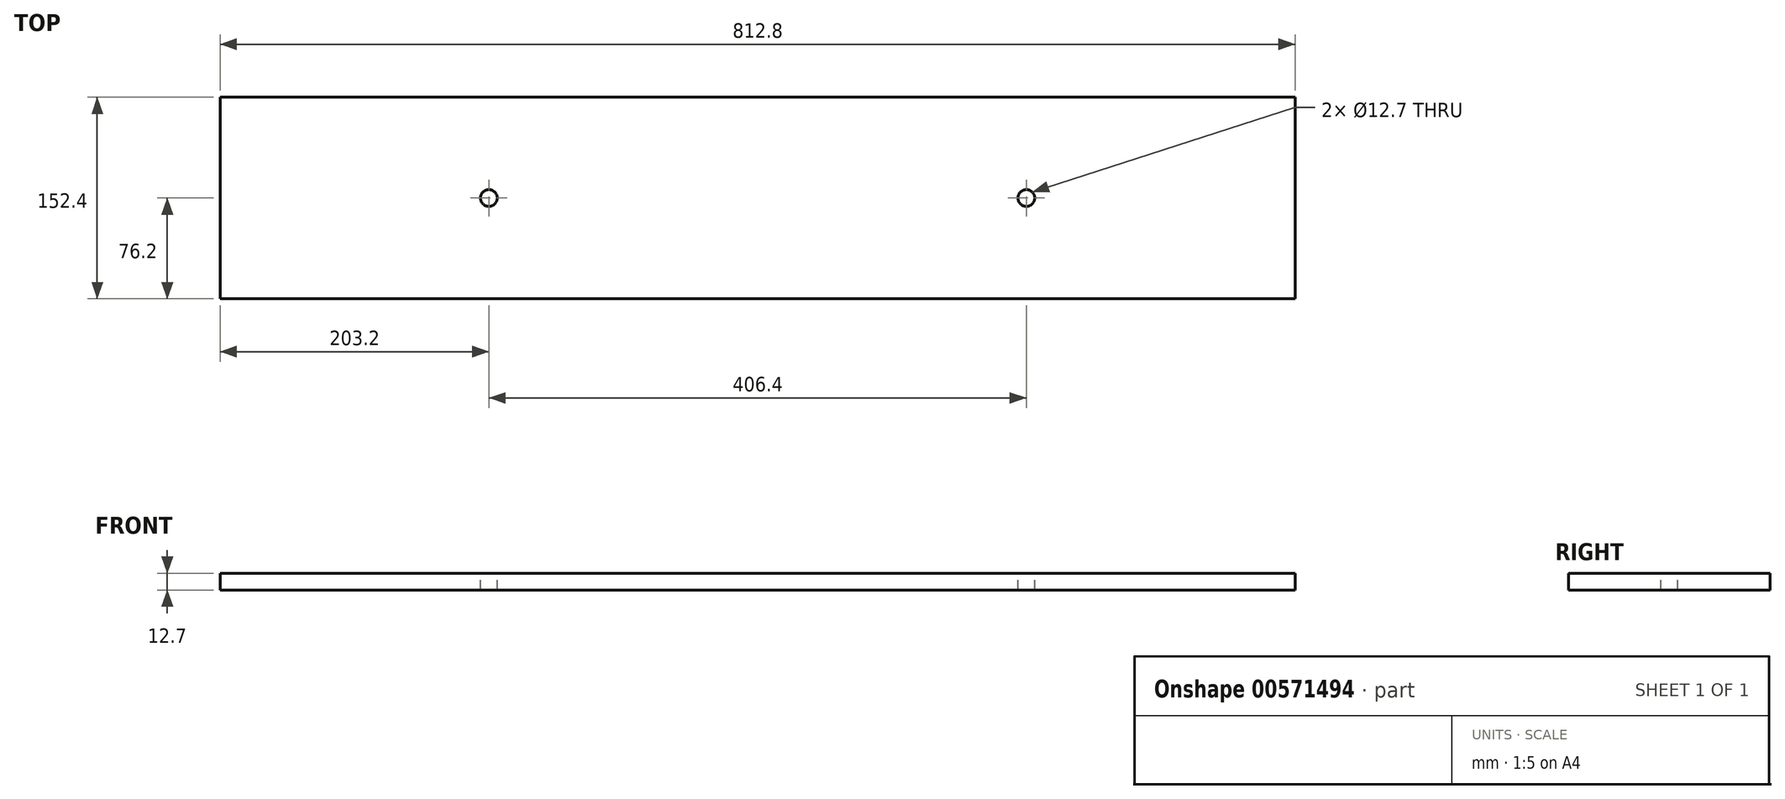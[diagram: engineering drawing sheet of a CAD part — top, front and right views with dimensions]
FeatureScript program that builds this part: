
annotation { "Feature Type Name" : "Feature", "Feature Type Description" : "" }
export const myFeature = defineFeature(function(context is Context, id is Id, definition is map)
    precondition{}
    {
        {
            var Q0;
            Q0=qCreatedBy(makeId("Top.planeOp"),FACE);
            var sketch = newSketch(context, id + "F0", { "sketchPlane" : qUnion([Q0])});
            skLineSegment(sketch, "E0.bottom", {"start": v(406.4, -76.2) * mm, "end": v(-406.4, -76.2) * mm});
            skLineSegment(sketch, "E0.top", {"start": v(406.4, 76.2) * mm, "end": v(-406.4, 76.2) * mm});
            skLineSegment(sketch, "E0.left", {"start": v(406.4, -76.2) * mm, "end": v(406.4, 76.2) * mm});
            skLineSegment(sketch, "E0.right", {"start": v(-406.4, -76.2) * mm, "end": v(-406.4, 76.2) * mm});
            skPoint(sketch, "E0.middle", {"position": v(0, 0) * mm});
            skSolve(sketch);
        }
        {
            var Q0;
            Q0 = qSketchRegion(id + "F0", true);
            extrude(context, id + "F1", {"entities" : qUnion([Q0]), "depth" : 12.7 * mm, "offsetDistance" : 25.4 * mm});
        }
        {
            var Q0;
            Q0=makeQuery(id+"F1.opExtrude","CAP_FACE",FACE,{"disambiguationData":[OSD([sQuery(id+"F0.wireOp",EDGE,"E0.bottom"),sQuery(id+"F0.wireOp",EDGE,"E0.top"),sQuery(id+"F0.wireOp",EDGE,"E0.left"),sQuery(id+"F0.wireOp",EDGE,"E0.right")])],"isStart":false});
            var sketch = newSketch(context, id + "F2", { "sketchPlane" : qUnion([Q0])});
            skCircle(sketch, "E1", {"center": v(-203.2, 0) * mm, "radius": 6.35 * mm});
            skCircle(sketch, "E2", {"center": v(203.2, 0) * mm, "radius": 6.35 * mm});
            skLineSegment(sketch, "E3", {"start": v(-203.2, 0) * mm, "end": v(-406.4, 0) * mm, "construction": true});
            skLineSegment(sketch, "E4", {"start": v(-203.2, 0) * mm, "end": v(0, 0) * mm, "construction": true});
            skSolve(sketch);
        }
        {
            var Q0;
            Q0 = qSketchRegion(id + "F2", true);
            extrude(context, id + "F3", {"entities" : qUnion([Q0]), "operationType" : NewBodyOperationType.REMOVE, "oppositeDirection" : true, "depth" : 25.4 * mm, "offsetDistance" : 25.4 * mm});
        }
    });
